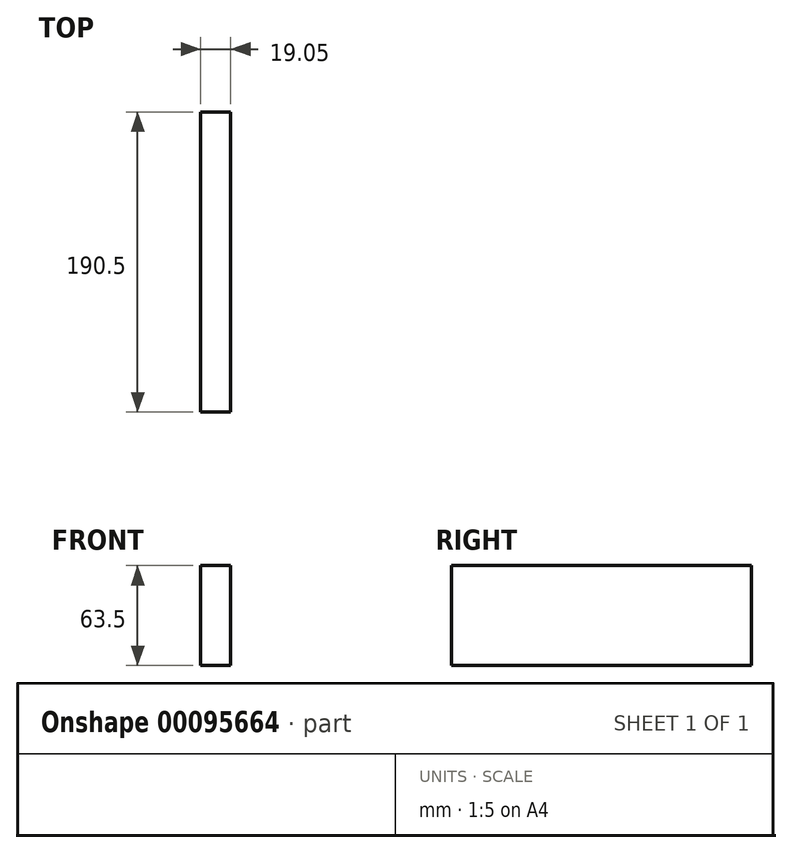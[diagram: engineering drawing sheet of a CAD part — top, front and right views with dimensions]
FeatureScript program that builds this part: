
annotation { "Feature Type Name" : "Feature", "Feature Type Description" : "" }
export const myFeature = defineFeature(function(context is Context, id is Id, definition is map)
    precondition{}
    {
        {
            var Q0;
            Q0=qCreatedBy(makeId("Right.planeOp"),FACE);
            var sketch = newSketch(context, id + "F0", { "sketchPlane" : qUnion([Q0])});
            skLineSegment(sketch, "E0.bottom", {"start": v(-436.58, -6.8) * mm, "end": v(-246.08, -6.8) * mm});
            skLineSegment(sketch, "E0.top", {"start": v(-436.58, -70.3) * mm, "end": v(-246.08, -70.3) * mm});
            skLineSegment(sketch, "E0.left", {"start": v(-436.58, -6.8) * mm, "end": v(-436.58, -70.3) * mm});
            skLineSegment(sketch, "E0.right", {"start": v(-246.08, -6.8) * mm, "end": v(-246.08, -70.3) * mm});
            skSolve(sketch);
        }
        {
            var Q0;
            Q0=makeQuery(id+"F0.imprint","IMPRINT",FACE,{"disambiguationData":[TD([[makeQuery(id+"F0.imprint","IMPRINT",EDGE,{"derivedFrom":sQuery(id+"F0.wireOp",EDGE,"E0.bottom")}),-1.0]])]});
            extrude(context, id + "F1", {"entities" : qUnion([Q0]), "depth" : 19.05 * mm});
        }
    });
